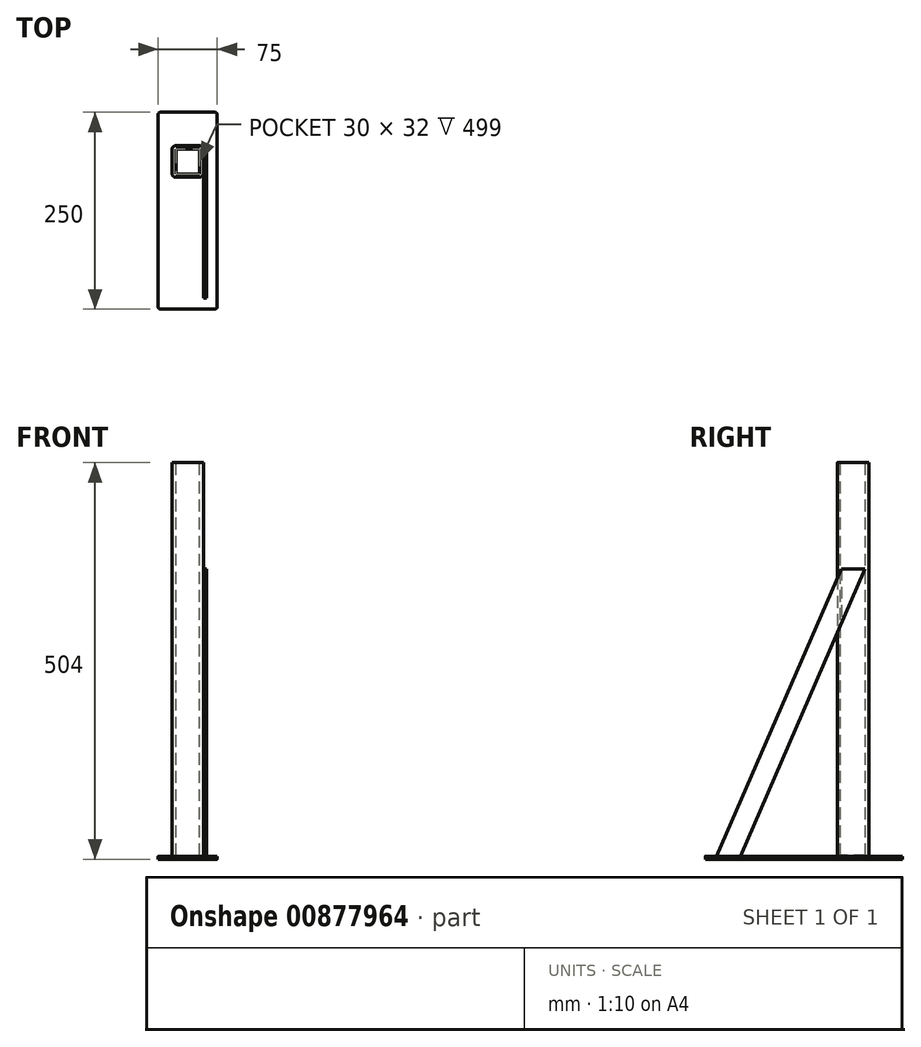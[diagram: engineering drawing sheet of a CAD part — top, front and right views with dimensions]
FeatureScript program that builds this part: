
annotation { "Feature Type Name" : "Feature", "Feature Type Description" : "" }
export const myFeature = defineFeature(function(context is Context, id is Id, definition is map)
    precondition{}
    {
        {
            var Q0;
            Q0=qCreatedBy(makeId("Top.planeOp"),FACE);
            var sketch = newSketch(context, id + "F0", { "sketchPlane" : qUnion([Q0])});
            skLineSegment(sketch, "E0.bottom", {"start": v(0, 0) * mm, "end": v(75, 0) * mm});
            skLineSegment(sketch, "E0.top", {"start": v(0, 250) * mm, "end": v(75, 250) * mm});
            skLineSegment(sketch, "E0.left", {"start": v(0, 0) * mm, "end": v(0, 250) * mm});
            skLineSegment(sketch, "E0.right", {"start": v(75, 0) * mm, "end": v(75, 250) * mm});
            skSolve(sketch);
        }
        {
            var Q0;
            Q0=makeQuery(id+"F0.imprint","IMPRINT",FACE,{"disambiguationData":[TD([[makeQuery(id+"F0.imprint","IMPRINT",EDGE,{"derivedFrom":sQuery(id+"F0.wireOp",EDGE,"E0.bottom")}),1.0]])]});
            extrude(context, id + "F1", {"entities" : qUnion([Q0]), "depth" : 4 * mm, "offsetDistance" : 25 * mm});
        }
        {
            var Q0;
            Q0=makeQuery(id+"F1.opExtrude","CAP_FACE",FACE,{"disambiguationData":[OSD([sQuery(id+"F0.wireOp",EDGE,"E0.bottom"),sQuery(id+"F0.wireOp",EDGE,"E0.top"),sQuery(id+"F0.wireOp",EDGE,"E0.left"),sQuery(id+"F0.wireOp",EDGE,"E0.right")])],"isStart":false});
            var sketch = newSketch(context, id + "F2", { "sketchPlane" : qUnion([Q0])});
            skLineSegment(sketch, "E1", {"start": v(0, 125) * mm, "end": v(75, 125) * mm, "construction": true});
            skLineSegment(sketch, "E2", {"start": v(37.5, 125) * mm, "end": v(37.5, 250) * mm, "construction": true});
            skLineSegment(sketch, "E3.bottom", {"start": v(17.5, 207.5) * mm, "end": v(57.5, 207.5) * mm});
            skLineSegment(sketch, "E3.top", {"start": v(17.5, 167.5) * mm, "end": v(57.5, 167.5) * mm});
            skLineSegment(sketch, "E3.left", {"start": v(17.5, 207.5) * mm, "end": v(17.5, 167.5) * mm});
            skLineSegment(sketch, "E3.right", {"start": v(57.5, 207.5) * mm, "end": v(57.5, 167.5) * mm});
            skPoint(sketch, "E3.middle", {"position": v(37.5, 187.5) * mm});
            skSolve(sketch);
        }
        {
            var Q0;
            Q0=makeQuery(id+"F2.imprint","IMPRINT",FACE,{"disambiguationData":[TD([[makeQuery(id+"F2.imprint","IMPRINT",EDGE,{"derivedFrom":sQuery(id+"F2.wireOp",EDGE,"E3.bottom")}),-1.0]])]});
            extrude(context, id + "F3", {"entities" : qUnion([Q0]), "operationType" : NewBodyOperationType.ADD, "depth" : 500 * mm, "offsetDistance" : 25 * mm});
        }
        {
            var Q0;
            Q0=makeQuery(id+"F3.opExtrude","CAP_FACE",FACE,{"disambiguationData":[OSD([sQuery(id+"F2.wireOp",EDGE,"E3.bottom"),sQuery(id+"F2.wireOp",EDGE,"E3.top"),sQuery(id+"F2.wireOp",EDGE,"E3.left"),sQuery(id+"F2.wireOp",EDGE,"E3.right")])],"isStart":false});
            var sketch = newSketch(context, id + "F4", { "sketchPlane" : qUnion([Q0])});
            skLineSegment(sketch, "E4", {"start": v(17.5, 207.5) * mm, "end": v(57.5, 167.5) * mm, "construction": true});
            skLineSegment(sketch, "E5.bottom", {"start": v(22.5, 203.5) * mm, "end": v(52.5, 203.5) * mm});
            skLineSegment(sketch, "E5.top", {"start": v(22.5, 171.5) * mm, "end": v(52.5, 171.5) * mm});
            skLineSegment(sketch, "E5.left", {"start": v(22.5, 203.5) * mm, "end": v(22.5, 171.5) * mm});
            skLineSegment(sketch, "E5.right", {"start": v(52.5, 203.5) * mm, "end": v(52.5, 171.5) * mm});
            skPoint(sketch, "E5.middle", {"position": v(37.5, 187.5) * mm});
            skSolve(sketch);
        }
        {
            var Q0;
            Q0=makeQuery(id+"F4.imprint","IMPRINT",FACE,{"disambiguationData":[TD([[makeQuery(id+"F4.imprint","IMPRINT",EDGE,{"derivedFrom":sQuery(id+"F4.wireOp",EDGE,"E5.bottom")}),-1.0]])]});
            extrude(context, id + "F5", {"entities" : qUnion([Q0]), "operationType" : NewBodyOperationType.REMOVE, "oppositeDirection" : true, "depth" : 499 * mm, "offsetDistance" : 25 * mm});
        }
        {
            var Q0;
            Q0=makeQuery(id+"F3.opExtrude","SWEPT_EDGE",EDGE,{"disambiguationData":[OSD([sQuery(id+"F2.wireOp",EDGE,"E3.top"),sQuery(id+"F2.wireOp",EDGE,"E3.right")])]});
            var Q1;
            Q1=makeQuery(id+"F3.opExtrude","SWEPT_EDGE",EDGE,{"disambiguationData":[OSD([sQuery(id+"F2.wireOp",EDGE,"E3.bottom"),sQuery(id+"F2.wireOp",EDGE,"E3.right")])]});
            var Q2;
            Q2=makeQuery(id+"F3.opExtrude","SWEPT_EDGE",EDGE,{"disambiguationData":[OSD([sQuery(id+"F2.wireOp",EDGE,"E3.bottom"),sQuery(id+"F2.wireOp",EDGE,"E3.left")])]});
            var Q3;
            Q3=makeQuery(id+"F3.opExtrude","SWEPT_EDGE",EDGE,{"disambiguationData":[OSD([sQuery(id+"F2.wireOp",EDGE,"E3.top"),sQuery(id+"F2.wireOp",EDGE,"E3.left")])]});
            fillet(context, id + "F6", {"entities" : qUnion([Q0, Q1, Q2, Q3]), "radius" : 5 * mm, "tangentPropagation" : true, "allowEdgeOverflow" : false});
        }
        {
            var Q0;
            Q0=makeQuery(id+"F1.opExtrude","SWEPT_EDGE",EDGE,{"disambiguationData":[OSD([sQuery(id+"F0.wireOp",EDGE,"E0.top"),sQuery(id+"F0.wireOp",EDGE,"E0.left")])]});
            var Q1;
            Q1=makeQuery(id+"F1.opExtrude","SWEPT_EDGE",EDGE,{"disambiguationData":[OSD([sQuery(id+"F0.wireOp",EDGE,"E0.bottom"),sQuery(id+"F0.wireOp",EDGE,"E0.left")])]});
            var Q2;
            Q2=makeQuery(id+"F1.opExtrude","SWEPT_EDGE",EDGE,{"disambiguationData":[OSD([sQuery(id+"F0.wireOp",EDGE,"E0.bottom"),sQuery(id+"F0.wireOp",EDGE,"E0.right")])]});
            var Q3;
            Q3=makeQuery(id+"F1.opExtrude","SWEPT_EDGE",EDGE,{"disambiguationData":[OSD([sQuery(id+"F0.wireOp",EDGE,"E0.top"),sQuery(id+"F0.wireOp",EDGE,"E0.right")])]});
            fillet(context, id + "F7", {"entities" : qUnion([Q0, Q1, Q2, Q3]), "radius" : 3 * mm, "tangentPropagation" : true, "allowEdgeOverflow" : false});
        }
        {
            var Q0;
            Q0=makeQuery(id+"F3.opExtrude","SWEPT_FACE",FACE,{"disambiguationData":[OSD([sQuery(id+"F2.wireOp",EDGE,"E3.right")])]});
            var sketch = newSketch(context, id + "F8", { "sketchPlane" : qUnion([Q0])});
            skLineSegment(sketch, "E6", {"start": v(187.5, 4) * mm, "end": v(0, 4) * mm, "construction": true});
            skLineSegment(sketch, "E7", {"start": v(202.5, 369.09) * mm, "end": v(44.28, 4) * mm, "construction": true});
            skLineSegment(sketch, "E8", {"start": v(202.5, 369.09) * mm, "end": v(172.5, 369.09) * mm, "construction": true});
            skLineSegment(sketch, "E9", {"start": v(44.28, 4) * mm, "end": v(14.28, 4) * mm, "construction": true});
            skLineSegment(sketch, "E10", {"start": v(14.28, 4) * mm, "end": v(172.5, 369.09) * mm, "construction": true});
            skLineSegment(sketch, "E11", {"start": v(14.28, 4) * mm, "end": v(44.28, 4) * mm});
            skLineSegment(sketch, "E12", {"start": v(44.28, 4) * mm, "end": v(202.5, 369.09) * mm});
            skLineSegment(sketch, "E13", {"start": v(172.5, 369.09) * mm, "end": v(14.28, 4) * mm});
            skLineSegment(sketch, "E14", {"start": v(202.5, 369.09) * mm, "end": v(172.5, 369.09) * mm});
            skSolve(sketch);
        }
        {
            var Q0;
            Q0 = qSketchRegion(id + "F8", true);
            extrude(context, id + "F9", {"entities" : qUnion([Q0]), "operationType" : NewBodyOperationType.ADD, "depth" : 4 * mm, "offsetDistance" : 25 * mm});
        }
    });
